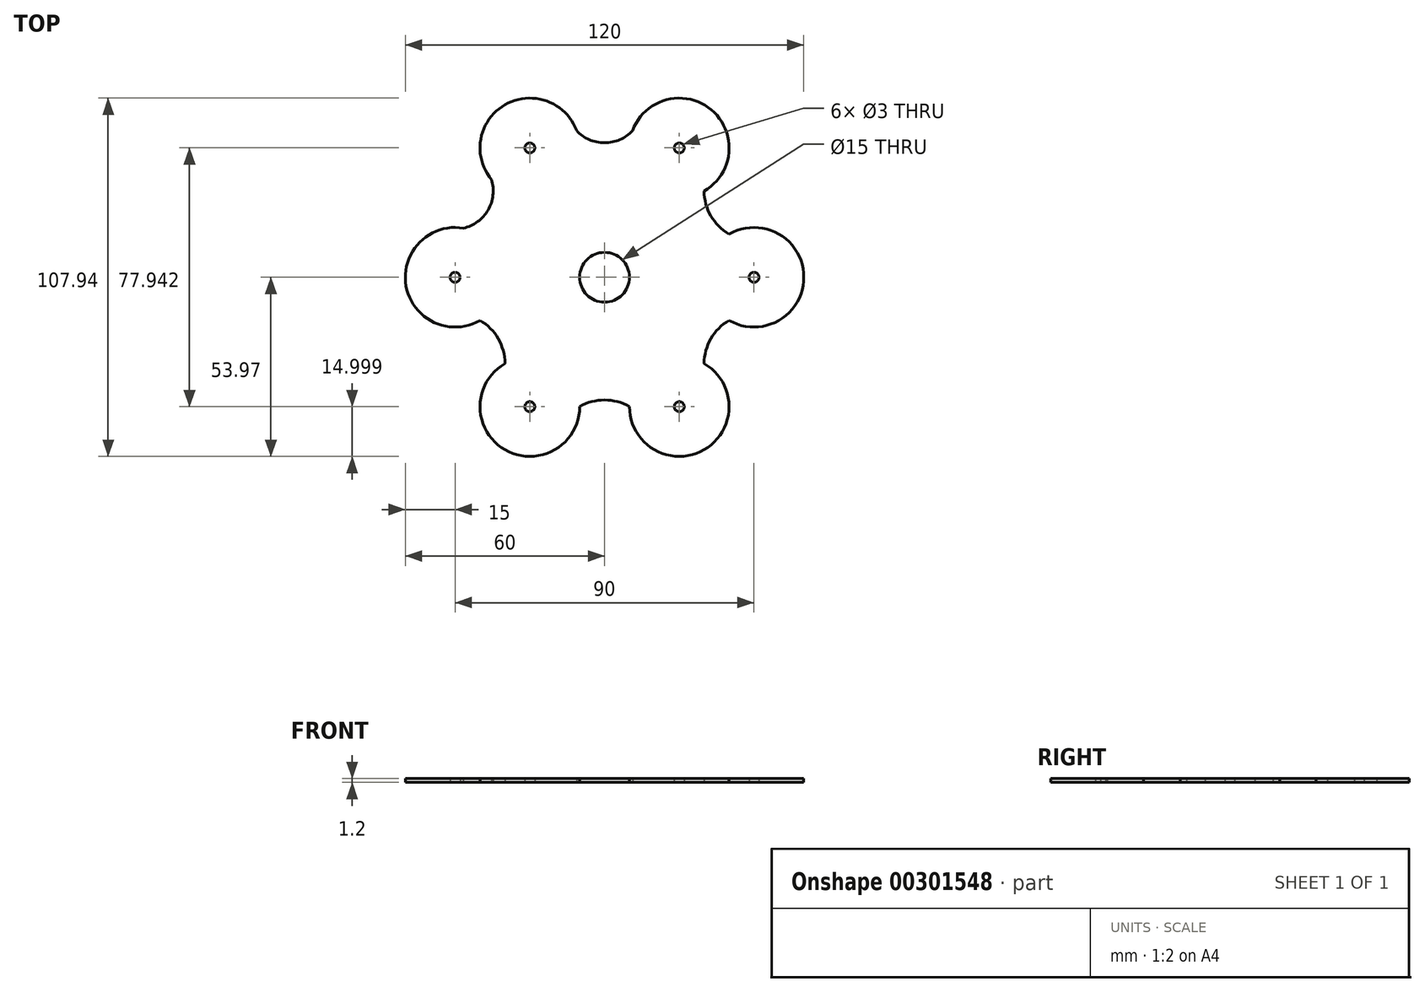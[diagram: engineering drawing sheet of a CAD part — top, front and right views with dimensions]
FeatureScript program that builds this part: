
annotation { "Feature Type Name" : "Feature", "Feature Type Description" : "" }
export const myFeature = defineFeature(function(context is Context, id is Id, definition is map)
    precondition{}
    {
        {
            var Q0;
            Q0=qCreatedBy(makeId("Top.planeOp"),FACE);
            var sketch = newSketch(context, id + "F0", { "sketchPlane" : qUnion([Q0])});
            skCircle(sketch, "E0", {"center": v(0, 0) * mm, "radius": 60 * mm, "construction": true});
            skCircle(sketch, "E1", {"center": v(0, 0) * mm, "radius": 7.5 * mm});
            skCircle(sketch, "E2", {"center": v(-22.5, -38.97) * mm, "radius": 1.5 * mm});
            skCircle(sketch, "E3", {"center": v(22.5, -38.97) * mm, "radius": 1.5 * mm});
            skCircle(sketch, "E4", {"center": v(22.5, 38.97) * mm, "radius": 1.5 * mm});
            skCircle(sketch, "E5", {"center": v(-22.5, 38.97) * mm, "radius": 1.5 * mm});
            skCircle(sketch, "E6", {"center": v(-45, 0) * mm, "radius": 1.5 * mm});
            skLineSegment(sketch, "E7", {"start": v(-22.5, -38.97) * mm, "end": v(-22.5, -38.97) * mm});
            skCircle(sketch, "E8.cCircle", {"center": v(0, 0) * mm, "radius": 45 * mm, "construction": true});
            skLineSegment(sketch, "E8.0", {"start": v(45, 0) * mm, "end": v(22.5, -38.97) * mm, "construction": true});
            skLineSegment(sketch, "E8.1", {"start": v(22.5, -38.97) * mm, "end": v(-22.5, -38.97) * mm, "construction": true});
            skLineSegment(sketch, "E8.2", {"start": v(-22.5, -38.97) * mm, "end": v(-45, 0) * mm, "construction": true});
            skLineSegment(sketch, "E8.3", {"start": v(-45, 0) * mm, "end": v(-22.5, 38.97) * mm, "construction": true});
            skLineSegment(sketch, "E8.4", {"start": v(-22.5, 38.97) * mm, "end": v(22.5, 38.97) * mm, "construction": true});
            skLineSegment(sketch, "E8.5", {"start": v(22.5, 38.97) * mm, "end": v(45, 0) * mm, "construction": true});
            skCircle(sketch, "E9", {"center": v(45, 0) * mm, "radius": 1.5 * mm});
            skLineSegment(sketch, "E10.0", {"start": v(60, 0) * mm, "end": v(30, -51.96) * mm, "construction": true});
            skLineSegment(sketch, "E10.1", {"start": v(30, -51.96) * mm, "end": v(-30, -51.96) * mm, "construction": true});
            skLineSegment(sketch, "E10.2", {"start": v(-30, -51.96) * mm, "end": v(-60, 0) * mm, "construction": true});
            skLineSegment(sketch, "E10.3", {"start": v(-60, 0) * mm, "end": v(-30, 51.96) * mm, "construction": true});
            skLineSegment(sketch, "E10.4", {"start": v(-30, 51.96) * mm, "end": v(30, 51.96) * mm, "construction": true});
            skLineSegment(sketch, "E10.5", {"start": v(30, 51.96) * mm, "end": v(60, 0) * mm, "construction": true});
            skCircle(sketch, "E11", {"center": v(-22.5, 38.97) * mm, "radius": 15 * mm});
            skCircle(sketch, "E12", {"center": v(22.5, 38.97) * mm, "radius": 15 * mm});
            skCircle(sketch, "E13", {"center": v(45, 0) * mm, "radius": 15 * mm});
            skCircle(sketch, "E14", {"center": v(22.5, -38.97) * mm, "radius": 15 * mm});
            skCircle(sketch, "E15", {"center": v(-22.5, -38.97) * mm, "radius": 15 * mm});
            skCircle(sketch, "E16", {"center": v(-45, 0) * mm, "radius": 15 * mm});
            skArc(sketch, "E17", {"start": v(-8.44, 44.2) * mm, "mid": v(0, 40.5) * mm, "end": v(8.44, 44.2) * mm});
            skLineSegment(sketch, "E18", {"start": v(-51.96, 30) * mm, "end": v(51.96, -30) * mm, "construction": true});
            skLineSegment(sketch, "E19", {"start": v(-51.96, -30) * mm, "end": v(51.96, 30) * mm, "construction": true});
            skArc(sketch, "E20", {"start": v(30, 25.98) * mm, "mid": v(32, 18.48) * mm, "end": v(37.5, 13) * mm});
            skArc(sketch, "E21", {"start": v(37.5, -13) * mm, "mid": v(32, -18.48) * mm, "end": v(30, -25.98) * mm});
            skArc(sketch, "E22", {"start": v(7.5, -38.97) * mm, "mid": v(0, -36.96) * mm, "end": v(-7.5, -38.97) * mm});
            skArc(sketch, "E23", {"start": v(-37.5, -13) * mm, "mid": v(-32, -18.48) * mm, "end": v(-30, -25.98) * mm});
            skArc(sketch, "E24", {"start": v(-34.06, 29.41) * mm, "mid": v(-35.07, 20.25) * mm, "end": v(-42.5, 14.8) * mm});
            skSolve(sketch);
        }
        {
            var Q0;
            Q0=makeQuery(id+"F0.imprint","IMPRINT",FACE,{"disambiguationData":[TD([[makeQuery(id+"F0.imprint","IMPRINT",EDGE,{"derivedFrom":sQuery(id+"F0.wireOp",EDGE,"E1")}),-1.0]])]});
            var Q1;
            Q1=makeQuery(id+"F0.imprint","IMPRINT",FACE,{"disambiguationData":[TD([[makeQuery(id+"F0.imprint","IMPRINT",EDGE,{"derivedFrom":sQuery(id+"F0.wireOp",EDGE,"E6")}),-1.0]])]});
            var Q2;
            Q2=makeQuery(id+"F0.imprint","IMPRINT",FACE,{"disambiguationData":[TD([[makeQuery(id+"F0.imprint","IMPRINT",EDGE,{"derivedFrom":sQuery(id+"F0.wireOp",EDGE,"E5")}),-1.0]])]});
            var Q3;
            Q3=makeQuery(id+"F0.imprint","IMPRINT",FACE,{"disambiguationData":[TD([[makeQuery(id+"F0.imprint","IMPRINT",EDGE,{"derivedFrom":sQuery(id+"F0.wireOp",EDGE,"E4")}),-1.0]])]});
            var Q4;
            Q4=makeQuery(id+"F0.imprint","IMPRINT",FACE,{"disambiguationData":[TD([[makeQuery(id+"F0.imprint","IMPRINT",EDGE,{"derivedFrom":sQuery(id+"F0.wireOp",EDGE,"E9")}),-1.0]])]});
            var Q5;
            Q5=makeQuery(id+"F0.imprint","IMPRINT",FACE,{"disambiguationData":[TD([[makeQuery(id+"F0.imprint","IMPRINT",EDGE,{"derivedFrom":sQuery(id+"F0.wireOp",EDGE,"E3")}),-1.0]])]});
            var Q6;
            Q6=makeQuery(id+"F0.imprint","IMPRINT",FACE,{"disambiguationData":[TD([[makeQuery(id+"F0.imprint","IMPRINT",EDGE,{"derivedFrom":sQuery(id+"F0.wireOp",EDGE,"E2")}),-1.0]])]});
            extrude(context, id + "F1", {"entities" : qUnion([Q0, Q1, Q2, Q3, Q4, Q5, Q6]), "depth" : 1.2 * mm});
        }
    });
